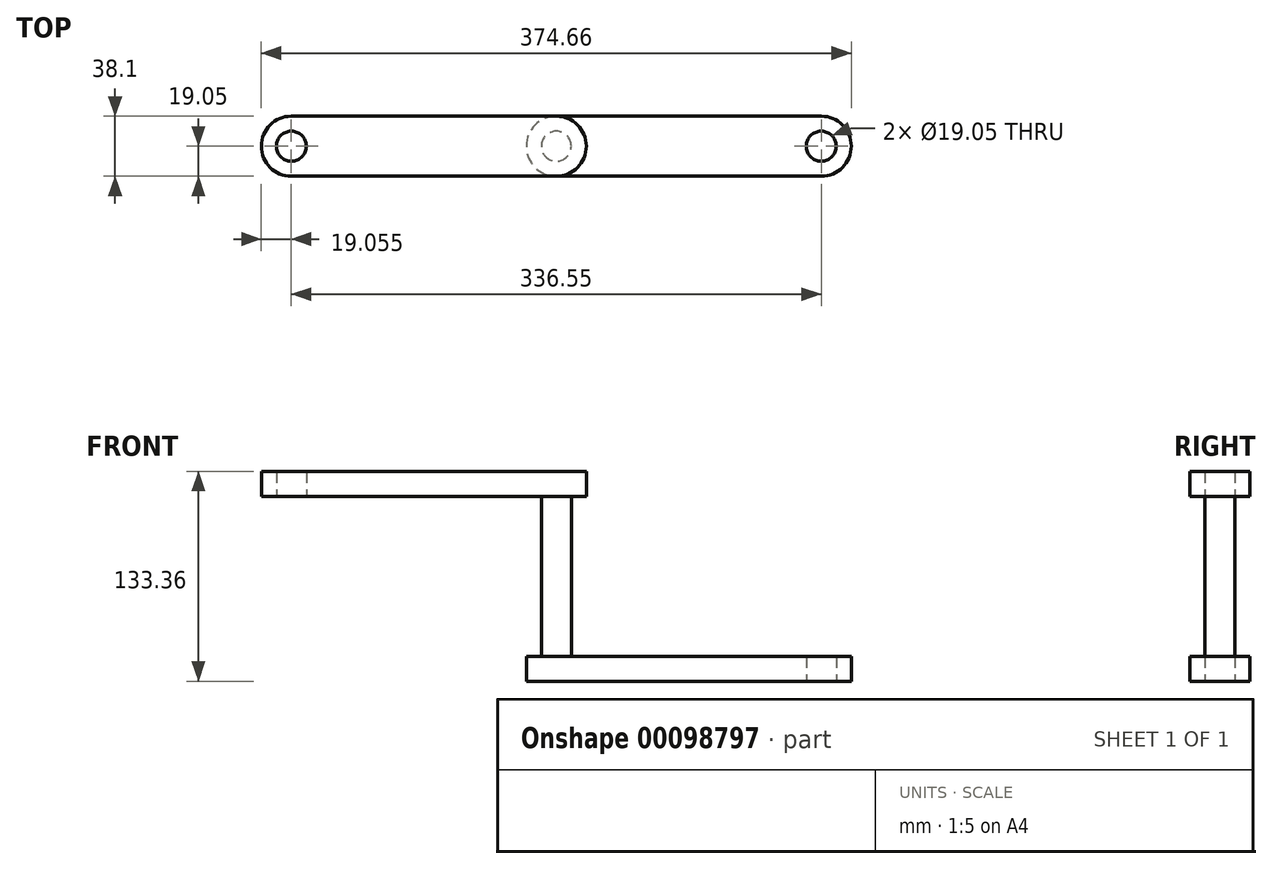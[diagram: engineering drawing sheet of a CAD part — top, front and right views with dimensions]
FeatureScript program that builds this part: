
annotation { "Feature Type Name" : "Feature", "Feature Type Description" : "" }
export const myFeature = defineFeature(function(context is Context, id is Id, definition is map)
    precondition{}
    {
        {
            var Q0;
            Q0=qCreatedBy(makeId("Front.planeOp"),FACE);
            var sketch = newSketch(context, id + "F0", { "sketchPlane" : qUnion([Q0])});
            skLineSegment(sketch, "E0.bottom", {"start": v(0, 0) * mm, "end": v(206.37, 0) * mm});
            skLineSegment(sketch, "E0.top", {"start": v(0, -15.87) * mm, "end": v(206.38, -15.87) * mm});
            skLineSegment(sketch, "E0.left", {"start": v(0, 0) * mm, "end": v(0, -15.87) * mm});
            skLineSegment(sketch, "E0.right", {"start": v(206.38, 0) * mm, "end": v(206.38, -15.87) * mm});
            skLineSegment(sketch, "E1.bottom", {"start": v(38.1, 101.6) * mm, "end": v(-168.28, 101.6) * mm});
            skLineSegment(sketch, "E1.top", {"start": v(38.1, 117.48) * mm, "end": v(-168.28, 117.47) * mm});
            skLineSegment(sketch, "E1.left", {"start": v(38.1, 101.6) * mm, "end": v(38.1, 117.48) * mm});
            skLineSegment(sketch, "E1.right", {"start": v(-168.28, 101.6) * mm, "end": v(-168.28, 117.47) * mm});
            skLineSegment(sketch, "E2", {"start": v(19.05, 94.09) * mm, "end": v(19.05, -42.4) * mm, "construction": true});
            skSolve(sketch);
        }
        {
            var Q0;
            Q0 = qSketchRegion(id + "F0", true);
            extrude(context, id + "F1", {"entities" : qUnion([Q0]), "depth" : 38.1 * mm});
        }
        {
            var Q0;
            Q0=makeQuery(id+"F1.opExtrude","CAP_EDGE",EDGE,{"disambiguationData":[OSD([sQuery(id+"F0.wireOp",EDGE,"E1.right")])],"isStart":false});
            var Q1;
            Q1=makeQuery(id+"F1.opExtrude","CAP_EDGE",EDGE,{"disambiguationData":[OSD([sQuery(id+"F0.wireOp",EDGE,"E1.right")])],"isStart":true});
            var Q2;
            Q2=makeQuery(id+"F1.opExtrude","CAP_EDGE",EDGE,{"disambiguationData":[OSD([sQuery(id+"F0.wireOp",EDGE,"E1.left")])],"isStart":false});
            var Q3;
            Q3=makeQuery(id+"F1.opExtrude","CAP_EDGE",EDGE,{"disambiguationData":[OSD([sQuery(id+"F0.wireOp",EDGE,"E1.left")])],"isStart":true});
            fillet(context, id + "F2", {"entities" : qUnion([Q0, Q1, Q2, Q3]), "radius" : 19.05 * mm, "tangentPropagation" : true, "allowEdgeOverflow" : false});
        }
        {
            var Q0;
            Q0=makeQuery(id+"F1.opExtrude","CAP_EDGE",EDGE,{"disambiguationData":[OSD([sQuery(id+"F0.wireOp",EDGE,"E0.left")])],"isStart":false});
            var Q1;
            Q1=makeQuery(id+"F1.opExtrude","CAP_EDGE",EDGE,{"disambiguationData":[OSD([sQuery(id+"F0.wireOp",EDGE,"E0.right")])],"isStart":false});
            var Q2;
            Q2=makeQuery(id+"F1.opExtrude","CAP_EDGE",EDGE,{"disambiguationData":[OSD([sQuery(id+"F0.wireOp",EDGE,"E0.right")])],"isStart":true});
            var Q3;
            Q3=makeQuery(id+"F1.opExtrude","CAP_EDGE",EDGE,{"disambiguationData":[OSD([sQuery(id+"F0.wireOp",EDGE,"E0.left")])],"isStart":true});
            fillet(context, id + "F3", {"entities" : qUnion([Q0, Q1, Q2, Q3]), "radius" : 19.05 * mm, "tangentPropagation" : true, "allowEdgeOverflow" : false});
        }
        {
            var Q0;
            Q0=makeQuery(id+"F1.opExtrude","SWEPT_FACE",FACE,{"disambiguationData":[OSD([sQuery(id+"F0.wireOp",EDGE,"E1.bottom")])]});
            var sketch = newSketch(context, id + "F4", { "sketchPlane" : qUnion([Q0])});
            skCircle(sketch, "E3", {"center": v(19.05, 19.05) * mm, "radius": 9.53 * mm});
            skSolve(sketch);
        }
        {
            var Q0;
            Q0 = qSketchRegion(id + "F4", true);
            extrude(context, id + "F5", {"entities" : qUnion([Q0]), "depth" : 101.6 * mm});
        }
        {
            var Q0;
            Q0=makeQuery(id+"F1.opExtrude","SWEPT_FACE",FACE,{"disambiguationData":[OSD([sQuery(id+"F0.wireOp",EDGE,"E1.bottom")])]});
            var sketch = newSketch(context, id + "F6", { "sketchPlane" : qUnion([Q0])});
            skCircle(sketch, "E4", {"center": v(-149.23, 19.05) * mm, "radius": 9.53 * mm});
            skSolve(sketch);
        }
        {
            var Q0;
            Q0=makeQuery(id+"F6.imprint","IMPRINT",FACE,{"disambiguationData":[TD([[makeQuery(id+"F6.imprint","IMPRINT",EDGE,{"derivedFrom":sQuery(id+"F6.wireOp",EDGE,"E4")}),1.0]])]});
            var Q1;
            Q1=sQuery(id+"F6.wireOp",EDGE,"E4");
            extrude(context, id + "F7", {"entities" : qUnion([Q0]), "operationType" : NewBodyOperationType.REMOVE, "surfaceEntities" : qUnion([Q1]), "oppositeDirection" : true, "depth" : 25.4 * mm});
        }
        {
            var Q0;
            Q0=makeQuery(id+"F1.opExtrude","SWEPT_FACE",FACE,{"disambiguationData":[OSD([sQuery(id+"F0.wireOp",EDGE,"E0.top")])]});
            var sketch = newSketch(context, id + "F8", { "sketchPlane" : qUnion([Q0])});
            skCircle(sketch, "E5", {"center": v(187.33, 19.05) * mm, "radius": 9.53 * mm});
            skSolve(sketch);
        }
        {
            var Q0;
            Q0=makeQuery(id+"F8.imprint","IMPRINT",FACE,{"disambiguationData":[TD([[makeQuery(id+"F8.imprint","IMPRINT",EDGE,{"derivedFrom":sQuery(id+"F8.wireOp",EDGE,"E5")}),1.0]])]});
            var Q1;
            Q1=sQuery(id+"F8.wireOp",EDGE,"E5");
            extrude(context, id + "F9", {"entities" : qUnion([Q0]), "operationType" : NewBodyOperationType.REMOVE, "surfaceEntities" : qUnion([Q1]), "oppositeDirection" : true, "depth" : 25.4 * mm});
        }
    });
